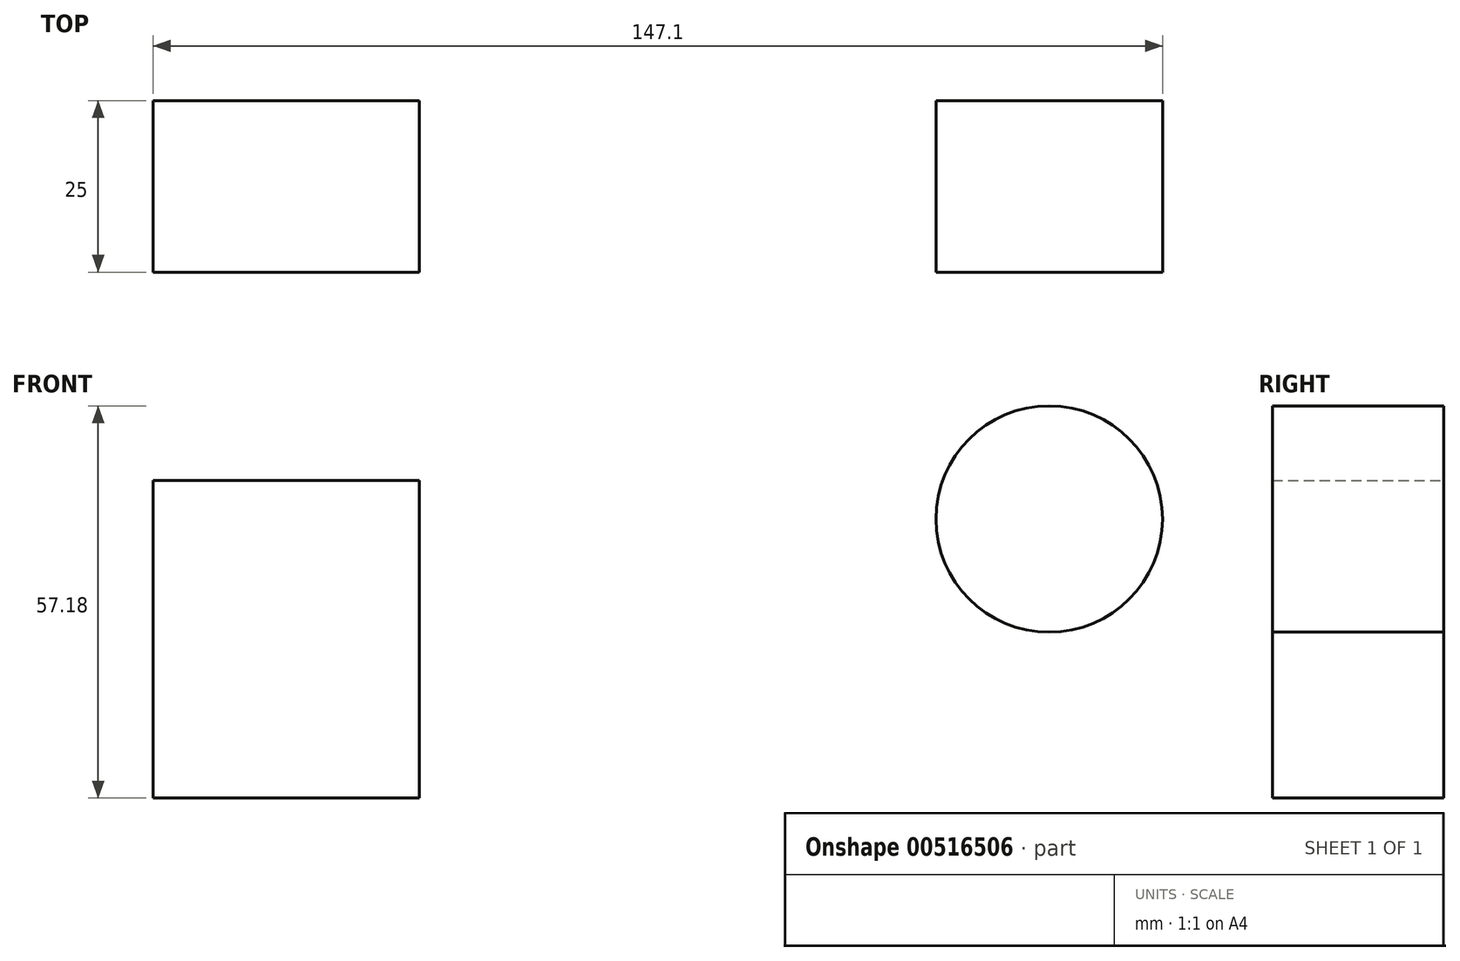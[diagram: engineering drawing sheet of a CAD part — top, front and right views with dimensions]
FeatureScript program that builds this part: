
annotation { "Feature Type Name" : "Feature", "Feature Type Description" : "" }
export const myFeature = defineFeature(function(context is Context, id is Id, definition is map)
    precondition{}
    {
        {
            var Q0;
            Q0=qCreatedBy(makeId("Front.planeOp"),FACE);
            var sketch = newSketch(context, id + "F0", { "sketchPlane" : qUnion([Q0])});
            skLineSegment(sketch, "E0.bottom", {"start": v(-66.72, 46.32) * mm, "end": v(-27.94, 46.32) * mm});
            skLineSegment(sketch, "E0.top", {"start": v(-66.72, 0) * mm, "end": v(-27.94, 0) * mm});
            skLineSegment(sketch, "E0.left", {"start": v(-66.72, 46.32) * mm, "end": v(-66.72, 0) * mm});
            skLineSegment(sketch, "E0.right", {"start": v(-27.94, 46.32) * mm, "end": v(-27.94, 0) * mm});
            skCircle(sketch, "E1", {"center": v(63.87, 40.68) * mm, "radius": 16.5 * mm});
            skSolve(sketch);
        }
        {
            var Q0;
            Q0 = qSketchRegion(id + "F0", true);
            extrude(context, id + "F1", {"entities" : qUnion([Q0]), "depth" : 25 * mm, "offsetDistance" : 25 * mm});
        }
    });
